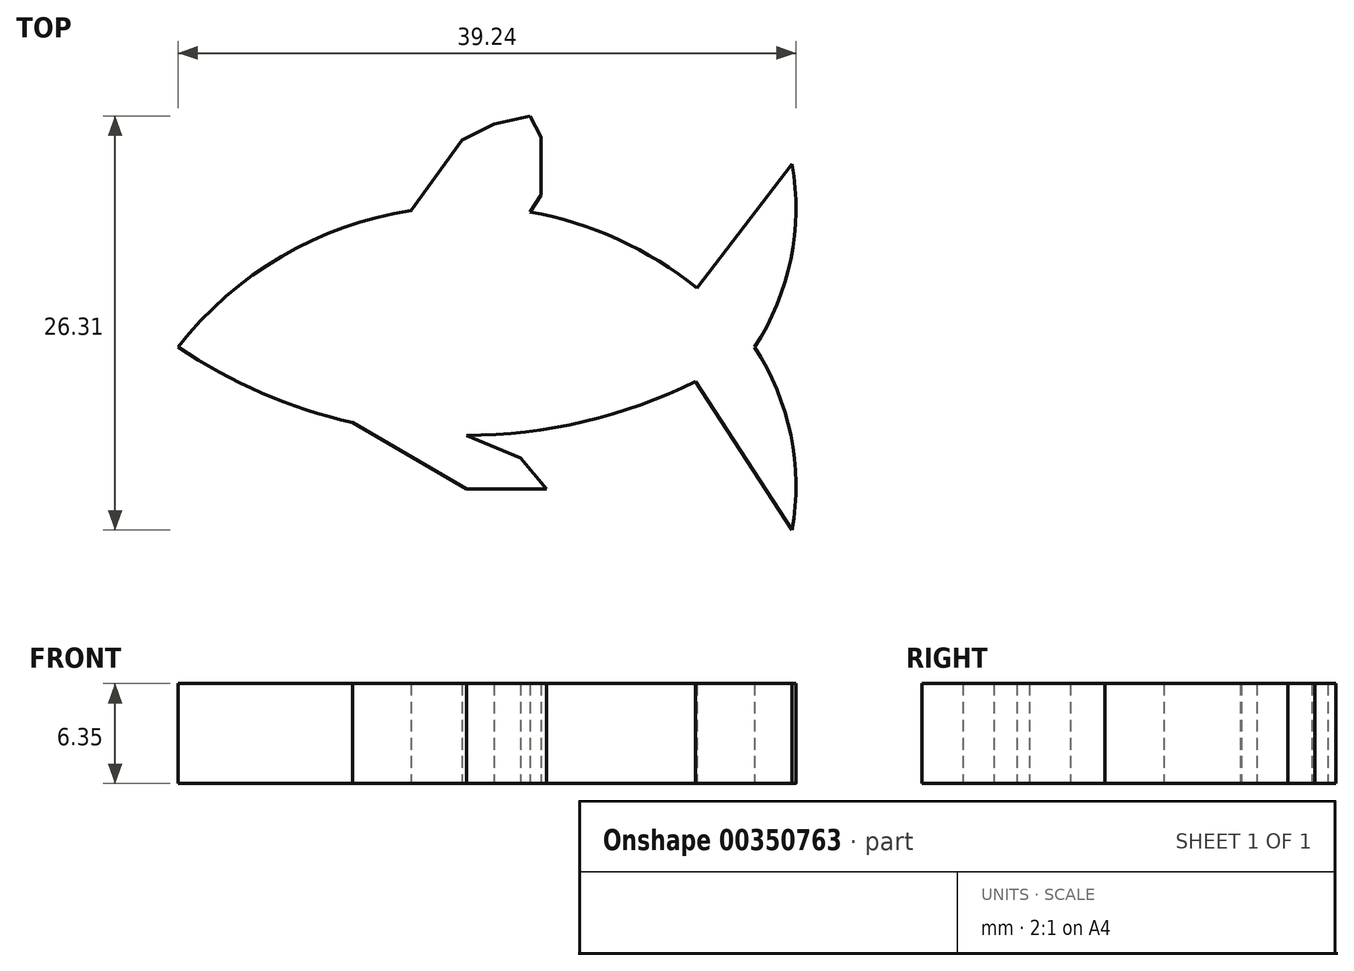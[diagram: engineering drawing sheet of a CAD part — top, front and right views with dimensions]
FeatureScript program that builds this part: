
annotation { "Feature Type Name" : "Feature", "Feature Type Description" : "" }
export const myFeature = defineFeature(function(context is Context, id is Id, definition is map)
    precondition{}
    {
        {
            var Q0;
            Q0=qCreatedBy(makeId("Top.planeOp"),FACE);
            var sketch = newSketch(context, id + "F0", { "sketchPlane" : qUnion([Q0])});
            skArc(sketch, "E0", {"start": v(36.61, 0) * mm, "mid": v(18.3, 8.95) * mm, "end": v(0, 0) * mm});
            skArc(sketch, "E1", {"start": v(0, 0) * mm, "mid": v(18.3, -5.6) * mm, "end": v(36.61, 0) * mm});
            skArc(sketch, "E2", {"start": v(36.61, 0) * mm, "mid": v(38.91, 5.59) * mm, "end": v(39, 11.62) * mm});
            skArc(sketch, "E3.MirrorCS", {"start": v(36.61, 0) * mm, "mid": v(38.91, -5.59) * mm, "end": v(39, -11.62) * mm});
            skPoint(sketch, "E4.endSnap0", {"position": v(18.3, 8.95) * mm});
            skLineSegment(sketch, "E5", {"start": v(16.55, 8.88) * mm, "end": v(20.08, 14.17) * mm});
            skLineSegment(sketch, "E6", {"start": v(18.51, 8.95) * mm, "end": v(22.34, 14.69) * mm});
            skLineSegment(sketch, "E7", {"start": v(20.08, 8.88) * mm, "end": v(23.05, 13.33) * mm});
            skLineSegment(sketch, "E8", {"start": v(22.34, 8.6) * mm, "end": v(23.05, 9.65) * mm});
            skLineSegment(sketch, "E9", {"start": v(14.8, 8.68) * mm, "end": v(18.02, 13.15) * mm});
            skLineSegment(sketch, "E10", {"start": v(18.02, 13.15) * mm, "end": v(20.08, 14.17) * mm});
            skLineSegment(sketch, "E11", {"start": v(20.08, 14.17) * mm, "end": v(22.34, 14.69) * mm});
            skLineSegment(sketch, "E12", {"start": v(22.34, 14.69) * mm, "end": v(23.05, 13.33) * mm});
            skLineSegment(sketch, "E13", {"start": v(23.05, 9.65) * mm, "end": v(23.05, 13.33) * mm});
            skLineSegment(sketch, "E14", {"start": v(11.08, -4.79) * mm, "end": v(18.3, -9.02) * mm});
            skPoint(sketch, "E14.endSnap0", {"position": v(18.3, -5.6) * mm});
            skLineSegment(sketch, "E15", {"start": v(15.92, -5.5) * mm, "end": v(21.79, -9.02) * mm});
            skLineSegment(sketch, "E16", {"start": v(21.79, -9.02) * mm, "end": v(18.3, -9.02) * mm});
            skLineSegment(sketch, "E17", {"start": v(17.44, -5.59) * mm, "end": v(23.4, -9.02) * mm});
            skLineSegment(sketch, "E18", {"start": v(23.4, -9.02) * mm, "end": v(21.79, -9.02) * mm});
            skLineSegment(sketch, "E19", {"start": v(18.3, -5.6) * mm, "end": v(21.76, -7.03) * mm});
            skLineSegment(sketch, "E20", {"start": v(21.76, -7.03) * mm, "end": v(23.4, -9.02) * mm});
            skLineSegment(sketch, "E21", {"start": v(39, 11.62) * mm, "end": v(32.95, 3.74) * mm});
            skLineSegment(sketch, "E22", {"start": v(39, -11.62) * mm, "end": v(32.86, -2.19) * mm});
            skSolve(sketch);
        }
        {
            var Q0;
            Q0 = qSketchRegion(id + "F0", true);
            extrude(context, id + "F1", {"entities" : qUnion([Q0]), "depth" : 6.35 * mm});
        }
    });
